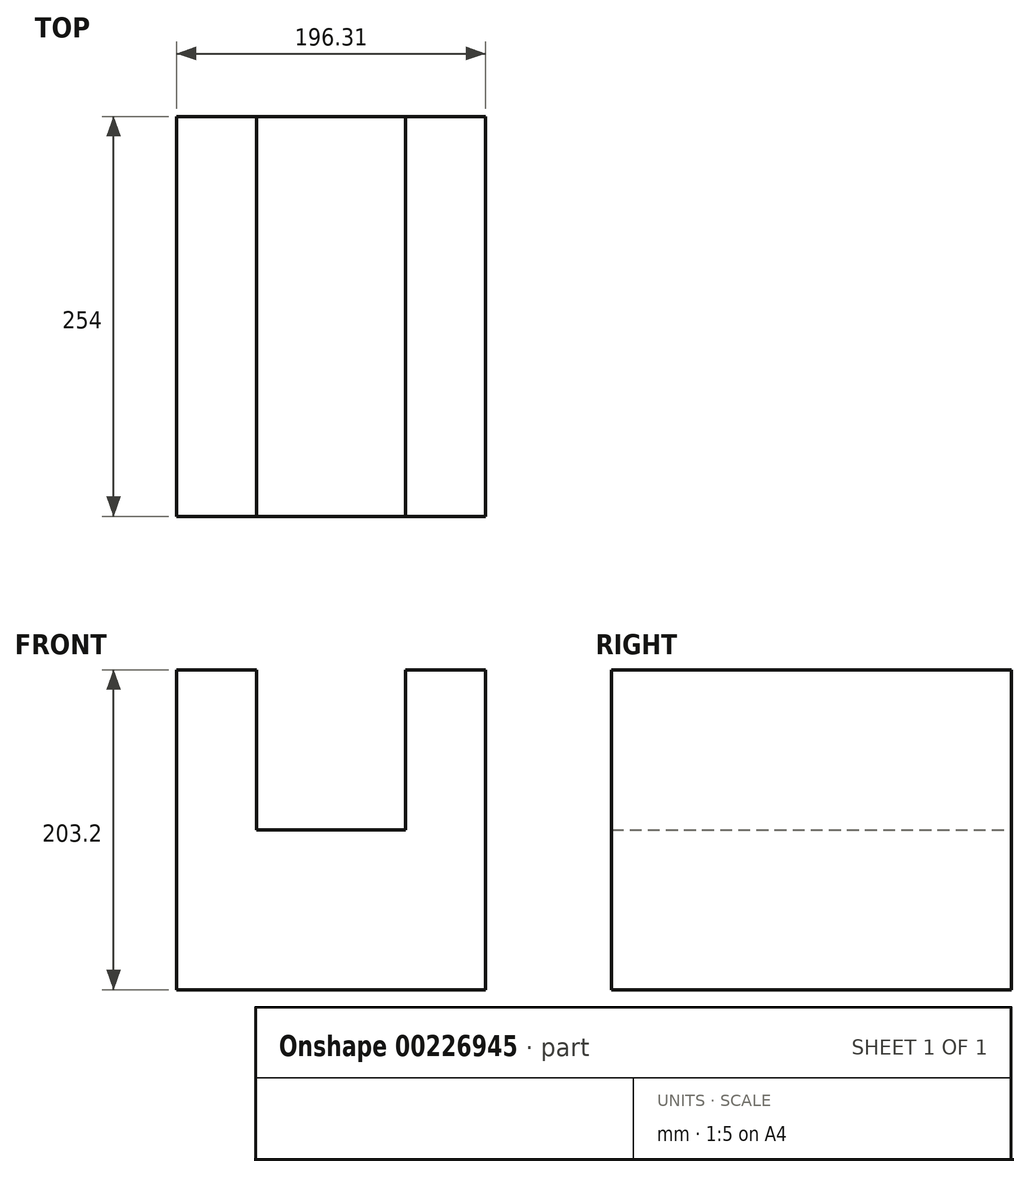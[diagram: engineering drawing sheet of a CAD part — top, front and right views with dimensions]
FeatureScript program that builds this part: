
annotation { "Feature Type Name" : "Feature", "Feature Type Description" : "" }
export const myFeature = defineFeature(function(context is Context, id is Id, definition is map)
    precondition{}
    {
        {
            var Q0;
            Q0=qCreatedBy(makeId("Front.planeOp"),FACE);
            var sketch = newSketch(context, id + "F0", { "sketchPlane" : qUnion([Q0])});
            skLineSegment(sketch, "E0.bottom", {"start": v(-96.63, 136.43) * mm, "end": v(-45.83, 136.43) * mm});
            skLineSegment(sketch, "E0.top", {"start": v(-96.63, -66.77) * mm, "end": v(99.68, -66.77) * mm});
            skLineSegment(sketch, "E0.left", {"start": v(-96.63, 136.43) * mm, "end": v(-96.63, -66.77) * mm});
            skLineSegment(sketch, "E0.right", {"start": v(99.68, 136.43) * mm, "end": v(99.68, -66.77) * mm});
            skLineSegment(sketch, "E1", {"start": v(-45.83, 136.43) * mm, "end": v(-45.83, 34.83) * mm});
            skLineSegment(sketch, "E2", {"start": v(-45.83, 34.83) * mm, "end": v(48.88, 34.83) * mm});
            skLineSegment(sketch, "E3", {"start": v(48.88, 34.83) * mm, "end": v(48.88, 136.43) * mm});
            skLineSegment(sketch, "E4.trimOffspring", {"start": v(48.88, 136.43) * mm, "end": v(99.68, 136.43) * mm});
            skSolve(sketch);
        }
        {
            var Q0;
            Q0 = qSketchRegion(id + "F0", true);
            extrude(context, id + "F1", {"entities" : qUnion([Q0]), "depth" : 254 * mm});
        }
    });
